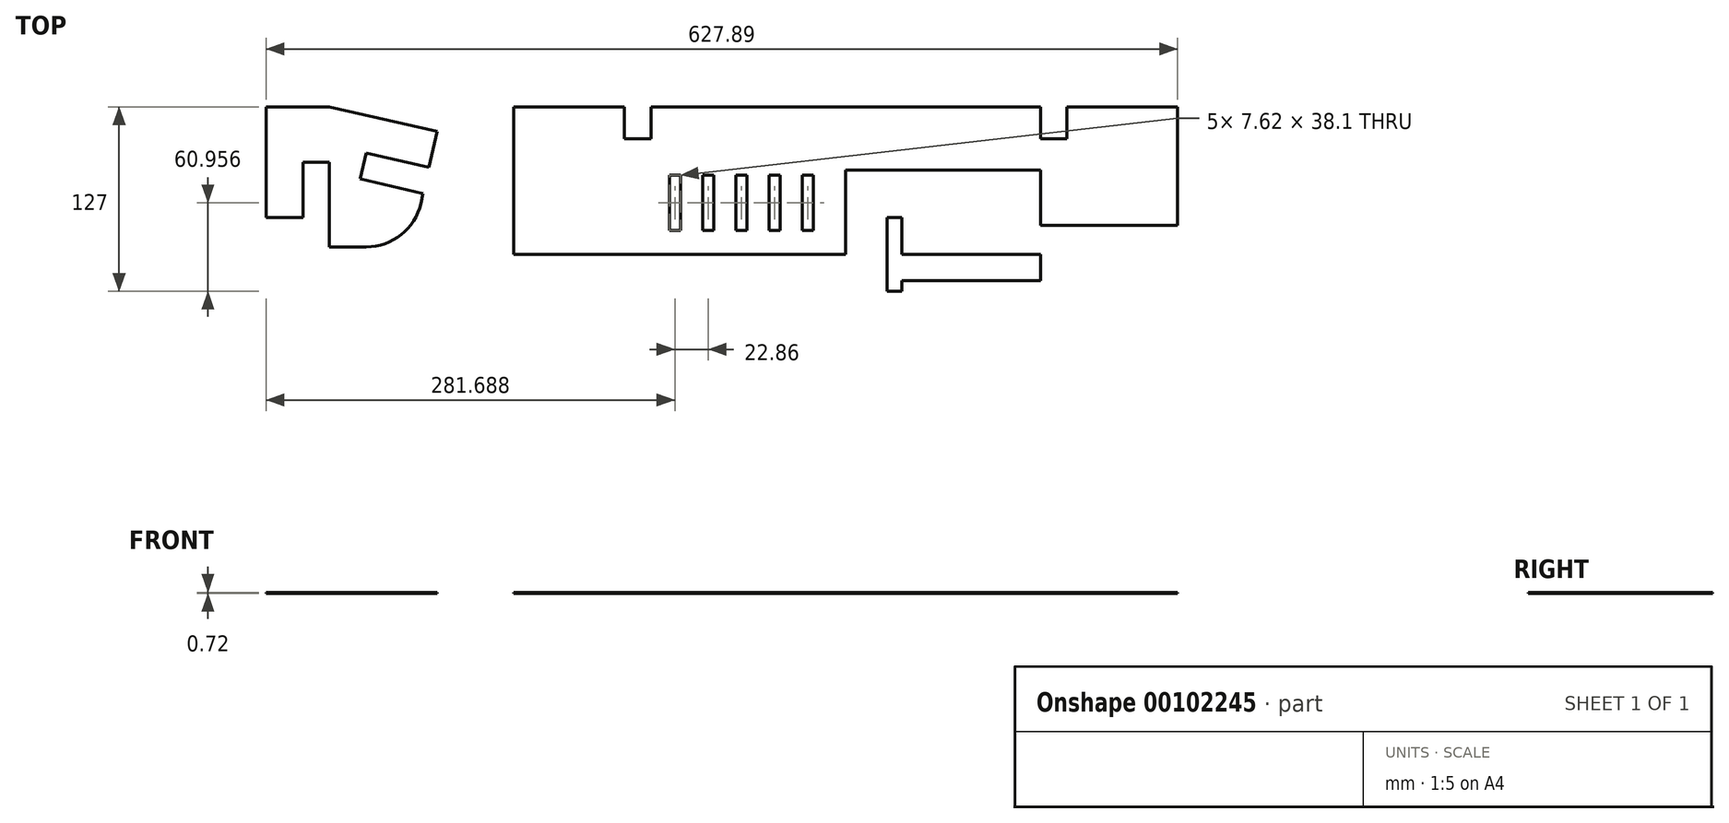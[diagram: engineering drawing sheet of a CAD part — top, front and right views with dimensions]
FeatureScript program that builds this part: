
annotation { "Feature Type Name" : "Feature", "Feature Type Description" : "" }
export const myFeature = defineFeature(function(context is Context, id is Id, definition is map)
    precondition{}
    {
        {
            assignVariable(context, id + "F0", {"name" : "ply34", "anyValue" : .72});
        }
        {
            var Q0;
            Q0=qCreatedBy(makeId("Top.planeOp"),FACE);
            var sketch = newSketch(context, id + "F1", { "sketchPlane" : qUnion([Q0])});
            skLineSegment(sketch, "E0", {"start": v(-43.69, -18.28) * mm, "end": v(-43.69, 19.82) * mm});
            skLineSegment(sketch, "E1", {"start": v(-43.69, 19.82) * mm, "end": v(-25.4, 19.82) * mm});
            skLineSegment(sketch, "E2.bottom", {"start": v(-43.69, -18.28) * mm, "end": v(-69.09, -18.28) * mm});
            skLineSegment(sketch, "E2.top", {"start": v(-43.69, 19.82) * mm, "end": v(-69.09, 19.82) * mm});
            skLineSegment(sketch, "E2.right", {"start": v(-69.09, -18.28) * mm, "end": v(-69.09, 19.82) * mm});
            skLineSegment(sketch, "E3.bottom", {"start": v(-69.09, 19.82) * mm, "end": v(-25.4, 19.82) * mm});
            skLineSegment(sketch, "E3.top", {"start": v(-69.09, 57.92) * mm, "end": v(-25.4, 57.92) * mm});
            skLineSegment(sketch, "E3.left", {"start": v(-69.09, 19.82) * mm, "end": v(-69.09, 57.92) * mm});
            skLineSegment(sketch, "E3.right", {"start": v(-25.4, 19.82) * mm, "end": v(-25.4, 57.92) * mm});
            skLineSegment(sketch, "E4", {"start": v(-25.4, 57.92) * mm, "end": v(48.88, 40.94) * mm});
            skLineSegment(sketch, "E5", {"start": v(48.88, 40.94) * mm, "end": v(37.56, -8.59) * mm});
            skLineSegment(sketch, "E6", {"start": v(37.56, -8.59) * mm, "end": v(-25.4, 5.8) * mm});
            skLineSegment(sketch, "E7", {"start": v(-25.4, 5.8) * mm, "end": v(-25.4, 19.82) * mm});
            skLineSegment(sketch, "E8", {"start": v(-25.4, 5.8) * mm, "end": v(-25.4, -38.53) * mm});
            skLineSegment(sketch, "E9", {"start": v(-25.4, -38.53) * mm, "end": v(0, -38.53) * mm});
            skLineSegment(sketch, "E10", {"start": v(0, -38.53) * mm, "end": v(0, 0) * mm});
            skLineSegment(sketch, "E11", {"start": v(43.22, 16.18) * mm, "end": v(-0.1, 26.08) * mm});
            skLineSegment(sketch, "E12", {"start": v(-0.1, 26.08) * mm, "end": v(-4.18, 8.25) * mm});
            skLineSegment(sketch, "E13", {"start": v(-4.18, 8.25) * mm, "end": v(39.15, -1.65) * mm});
            skArc(sketch, "E14", {"start": v(0, -38.53) * mm, "mid": v(24.02, -30.13) * mm, "end": v(37.56, -8.59) * mm});
            skLineSegment(sketch, "E15.bottom", {"start": v(101.6, 57.92) * mm, "end": v(558.8, 57.92) * mm});
            skLineSegment(sketch, "E15.top", {"start": v(101.6, -43.68) * mm, "end": v(464.31, -43.68) * mm});
            skLineSegment(sketch, "E15.left", {"start": v(101.6, 57.92) * mm, "end": v(101.6, -43.68) * mm});
            skLineSegment(sketch, "E15.right", {"start": v(558.8, 57.92) * mm, "end": v(558.8, -43.68) * mm});
            skLineSegment(sketch, "E16.bottom", {"start": v(177.8, 57.92) * mm, "end": v(196.09, 57.92) * mm});
            skLineSegment(sketch, "E16.top", {"start": v(177.8, 36.15) * mm, "end": v(196.09, 36.15) * mm});
            skLineSegment(sketch, "E16.left", {"start": v(177.8, 57.92) * mm, "end": v(177.8, 36.15) * mm});
            skLineSegment(sketch, "E16.right", {"start": v(196.09, 57.92) * mm, "end": v(196.09, 36.15) * mm});
            skLineSegment(sketch, "E17.bottom", {"start": v(464.31, 57.92) * mm, "end": v(482.6, 57.92) * mm});
            skLineSegment(sketch, "E17.top", {"start": v(464.31, 36.15) * mm, "end": v(482.6, 36.15) * mm});
            skLineSegment(sketch, "E17.left", {"start": v(464.31, 57.92) * mm, "end": v(464.31, 36.15) * mm});
            skLineSegment(sketch, "E17.right", {"start": v(482.6, 57.92) * mm, "end": v(482.6, 36.15) * mm});
            skLineSegment(sketch, "E18", {"start": v(-4.18, 8.25) * mm, "end": v(-25.4, 13.1) * mm, "construction": true});
            skLineSegment(sketch, "E19", {"start": v(330.2, 57.92) * mm, "end": v(330.2, -43.68) * mm, "construction": true});
            skLineSegment(sketch, "E20.bottom", {"start": v(216.4, 10.93) * mm, "end": v(208.79, 10.93) * mm});
            skLineSegment(sketch, "E20.top", {"start": v(216.4, -27.17) * mm, "end": v(208.79, -27.17) * mm});
            skLineSegment(sketch, "E20.left", {"start": v(216.4, 10.93) * mm, "end": v(216.4, -27.17) * mm});
            skLineSegment(sketch, "E20.right", {"start": v(208.79, 10.93) * mm, "end": v(208.79, -27.17) * mm});
            skPoint(sketch, "E20.middle", {"position": v(212.6, -8.12) * mm});
            skLineSegment(sketch, "E21.bottom", {"start": v(177.8, 36.15) * mm, "end": v(196.09, 36.15) * mm, "construction": true});
            skLineSegment(sketch, "E21.top", {"start": v(177.8, -8.12) * mm, "end": v(196.09, -8.12) * mm, "construction": true});
            skLineSegment(sketch, "E21.left", {"start": v(177.8, 36.15) * mm, "end": v(177.8, -8.12) * mm, "construction": true});
            skLineSegment(sketch, "E21.right", {"start": v(196.09, 36.15) * mm, "end": v(196.09, -8.12) * mm, "construction": true});
            skLineSegment(sketch, "E22.bottom", {"start": v(464.31, 36.15) * mm, "end": v(482.6, 36.15) * mm, "construction": true});
            skLineSegment(sketch, "E22.top", {"start": v(464.31, -8.12) * mm, "end": v(482.6, -8.12) * mm, "construction": true});
            skLineSegment(sketch, "E22.left", {"start": v(464.31, 36.15) * mm, "end": v(464.31, -8.12) * mm, "construction": true});
            skLineSegment(sketch, "E22.right", {"start": v(482.6, 36.15) * mm, "end": v(482.6, -8.12) * mm, "construction": true});
            skLineSegment(sketch, "E23.bottom", {"start": v(231.65, 10.93) * mm, "end": v(239.27, 10.93) * mm});
            skLineSegment(sketch, "E23.top", {"start": v(231.65, -27.17) * mm, "end": v(239.27, -27.17) * mm});
            skLineSegment(sketch, "E23.left", {"start": v(231.65, 10.93) * mm, "end": v(231.65, -27.17) * mm});
            skLineSegment(sketch, "E23.right", {"start": v(239.27, 10.93) * mm, "end": v(239.27, -27.17) * mm});
            skLineSegment(sketch, "E24.bottom", {"start": v(254.5, -27.17) * mm, "end": v(262.13, -27.17) * mm});
            skLineSegment(sketch, "E24.top", {"start": v(254.5, 10.93) * mm, "end": v(262.13, 10.93) * mm});
            skLineSegment(sketch, "E24.left", {"start": v(254.5, -27.17) * mm, "end": v(254.5, 10.93) * mm});
            skLineSegment(sketch, "E24.right", {"start": v(262.13, -27.17) * mm, "end": v(262.13, 10.93) * mm});
            skLineSegment(sketch, "E25.bottom", {"start": v(277.37, -27.17) * mm, "end": v(284.99, -27.17) * mm});
            skLineSegment(sketch, "E25.top", {"start": v(277.37, 10.93) * mm, "end": v(284.99, 10.93) * mm});
            skLineSegment(sketch, "E25.left", {"start": v(277.37, -27.17) * mm, "end": v(277.37, 10.93) * mm});
            skLineSegment(sketch, "E25.right", {"start": v(284.99, -27.17) * mm, "end": v(284.99, 10.93) * mm});
            skLineSegment(sketch, "E26.bottom", {"start": v(300.23, -27.17) * mm, "end": v(307.85, -27.17) * mm});
            skLineSegment(sketch, "E26.top", {"start": v(300.23, 10.93) * mm, "end": v(307.85, 10.93) * mm});
            skLineSegment(sketch, "E26.left", {"start": v(300.23, -27.17) * mm, "end": v(300.23, 10.93) * mm});
            skLineSegment(sketch, "E26.right", {"start": v(307.85, -27.17) * mm, "end": v(307.85, 10.93) * mm});
            skLineSegment(sketch, "E27", {"start": v(196.09, -8.12) * mm, "end": v(464.31, -8.12) * mm, "construction": true});
            skLineSegment(sketch, "E28.bottom", {"start": v(558.8, -23.71) * mm, "end": v(368.94, -23.71) * mm});
            skLineSegment(sketch, "E28.top", {"start": v(558.8, -61.81) * mm, "end": v(368.94, -61.81) * mm});
            skLineSegment(sketch, "E28.right", {"start": v(368.94, -23.71) * mm, "end": v(368.94, -61.81) * mm});
            skLineSegment(sketch, "E29.bottom", {"start": v(558.8, -23.71) * mm, "end": v(482.6, -23.71) * mm});
            skLineSegment(sketch, "E29.top", {"start": v(558.8, 14.39) * mm, "end": v(482.6, 14.39) * mm});
            skLineSegment(sketch, "E29.left", {"start": v(558.8, -23.71) * mm, "end": v(558.8, 14.39) * mm});
            skLineSegment(sketch, "E29.right", {"start": v(482.6, -23.71) * mm, "end": v(482.6, 14.39) * mm});
            skLineSegment(sketch, "E30.bottom", {"start": v(464.31, 14.39) * mm, "end": v(368.94, 14.39) * mm});
            skLineSegment(sketch, "E30.top", {"start": v(464.31, -23.71) * mm, "end": v(368.94, -23.71) * mm});
            skLineSegment(sketch, "E30.left", {"start": v(464.31, 14.39) * mm, "end": v(464.31, -23.71) * mm});
            skLineSegment(sketch, "E30.right", {"start": v(368.94, 14.39) * mm, "end": v(368.94, -23.71) * mm});
            skLineSegment(sketch, "E31.bottom", {"start": v(368.94, 14.39) * mm, "end": v(330.2, 14.39) * mm});
            skLineSegment(sketch, "E31.top", {"start": v(368.94, -43.68) * mm, "end": v(330.2, -43.68) * mm});
            skLineSegment(sketch, "E31.left", {"start": v(368.94, 14.39) * mm, "end": v(368.94, -43.68) * mm});
            skLineSegment(sketch, "E31.right", {"start": v(330.2, 14.39) * mm, "end": v(330.2, -43.68) * mm});
            skLineSegment(sketch, "E32.bottom", {"start": v(368.94, -18.28) * mm, "end": v(358.78, -18.28) * mm});
            skLineSegment(sketch, "E32.top", {"start": v(368.94, -69.08) * mm, "end": v(358.78, -69.08) * mm});
            skLineSegment(sketch, "E32.left", {"start": v(368.94, -18.28) * mm, "end": v(368.94, -69.08) * mm});
            skLineSegment(sketch, "E32.right", {"start": v(358.78, -18.28) * mm, "end": v(358.78, -69.08) * mm});
            skPoint(sketch, "E33", {"position": v(358.78, -43.68) * mm});
            skLineSegment(sketch, "E34.bottom", {"start": v(464.31, -23.71) * mm, "end": v(558.8, -23.71) * mm});
            skLineSegment(sketch, "E34.top", {"start": v(464.31, -61.81) * mm, "end": v(558.8, -61.81) * mm});
            skLineSegment(sketch, "E34.left", {"start": v(464.31, -23.71) * mm, "end": v(464.31, -61.81) * mm});
            skLineSegment(sketch, "E34.right", {"start": v(558.8, -23.71) * mm, "end": v(558.8, -43.68) * mm});
            skLineSegment(sketch, "E35", {"start": v(558.8, -43.68) * mm, "end": v(558.8, -61.81) * mm});
            skSolve(sketch);
        }
        {
            var Q0;
            Q0=makeQuery(id+"F1.imprint","IMPRINT",FACE,{"disambiguationData":[TD([[makeQuery(id+"F1.imprint","IMPRINT",EDGE,{"derivedFrom":sQuery(id+"F1.wireOp",EDGE,"E3.right")}),-1.0]])]});
            var Q1;
            {var subQ2=sQuery(id+"F1.wireOp",EDGE,"E10");Q1=makeQuery(id+"F1.imprint","IMPRINT",FACE,{"disambiguationData":[TD([[makeQuery(id+"F1.imprint","IMPRINT",EDGE,{"derivedFrom":subQ2}),-1.0]])]});}
            var Q2;
            Q2=makeQuery(id+"F1.imprint","IMPRINT",FACE,{"disambiguationData":[TD([[makeQuery(id+"F1.imprint","IMPRINT",EDGE,{"derivedFrom":sQuery(id+"F1.wireOp",EDGE,"E3.top")}),-1.0]])]});
            var Q3;
            Q3=makeQuery(id+"F1.imprint","IMPRINT",FACE,{"disambiguationData":[TD([[makeQuery(id+"F1.imprint","IMPRINT",EDGE,{"derivedFrom":sQuery(id+"F1.wireOp",EDGE,"E2.bottom")}),-1.0]])]});
            var Q4;
            {var subQ0=sQuery(id+"F1.wireOp",EDGE,"E8");Q4=makeQuery(id+"F1.imprint","IMPRINT",FACE,{"disambiguationData":[TD([[makeQuery(id+"F1.imprint","IMPRINT",EDGE,{"derivedFrom":subQ0}),1.0]])]});}
            var Q5;
            {var subQ2=sQuery(id+"F1.wireOp",EDGE,"E15.left");Q5=makeQuery(id+"F1.imprint","IMPRINT",FACE,{"disambiguationData":[TD([[makeQuery(id+"F1.imprint","IMPRINT",EDGE,{"derivedFrom":subQ2}),1.0]])]});}
            var Q6;
            {var subQ6=sQuery(id+"F1.wireOp",EDGE,"E32.bottom");Q6=makeQuery(id+"F1.imprint","IMPRINT",FACE,{"disambiguationData":[TD([[makeQuery(id+"F1.imprint","IMPRINT",EDGE,{"derivedFrom":subQ6}),1.0]])]});}
            var Q7;
            {var subQ2=sQuery(id+"F1.wireOp",EDGE,"E32.top");Q7=makeQuery(id+"F1.imprint","IMPRINT",FACE,{"disambiguationData":[TD([[makeQuery(id+"F1.imprint","IMPRINT",EDGE,{"derivedFrom":subQ2}),-1.0]])]});}
            var Q8;
            {var subQ5=sQuery(id+"F1.wireOp",EDGE,"E28.top");Q8=makeQuery(id+"F1.imprint","IMPRINT",FACE,{"disambiguationData":[TD([[makeQuery(id+"F1.imprint","IMPRINT",EDGE,{"derivedFrom":subQ5}),-1.0]])]});}
            var Q9;
            {var subQ5=sQuery(id+"F1.wireOp",EDGE,"E30.top");Q9=makeQuery(id+"F1.imprint","IMPRINT",FACE,{"disambiguationData":[TD([[makeQuery(id+"F1.imprint","IMPRINT",EDGE,{"derivedFrom":subQ5}),1.0]])]});}
            var Q10;
            {var subQ4=sQuery(id+"F1.wireOp",EDGE,"E34.top");Q10=makeQuery(id+"F1.imprint","IMPRINT",FACE,{"disambiguationData":[TD([[makeQuery(id+"F1.imprint","IMPRINT",EDGE,{"derivedFrom":subQ4}),1.0]])]});}
            var Q11;
            Q11=makeQuery(id+"F1.imprint","IMPRINT",FACE,{"disambiguationData":[TD([[makeQuery(id+"F1.imprint","IMPRINT",EDGE,{"derivedFrom":sQuery(id+"F1.wireOp",EDGE,"E29.top")}),1.0]])]});
            extrude(context, id + "F2", {"entities" : qUnion([Q0, Q1, Q2, Q3, Q4, Q5, Q6, Q7, Q8, Q9, Q10, Q11]), "depth" : (getVariable(context, 'ply34')) * mm});
        }
    });
